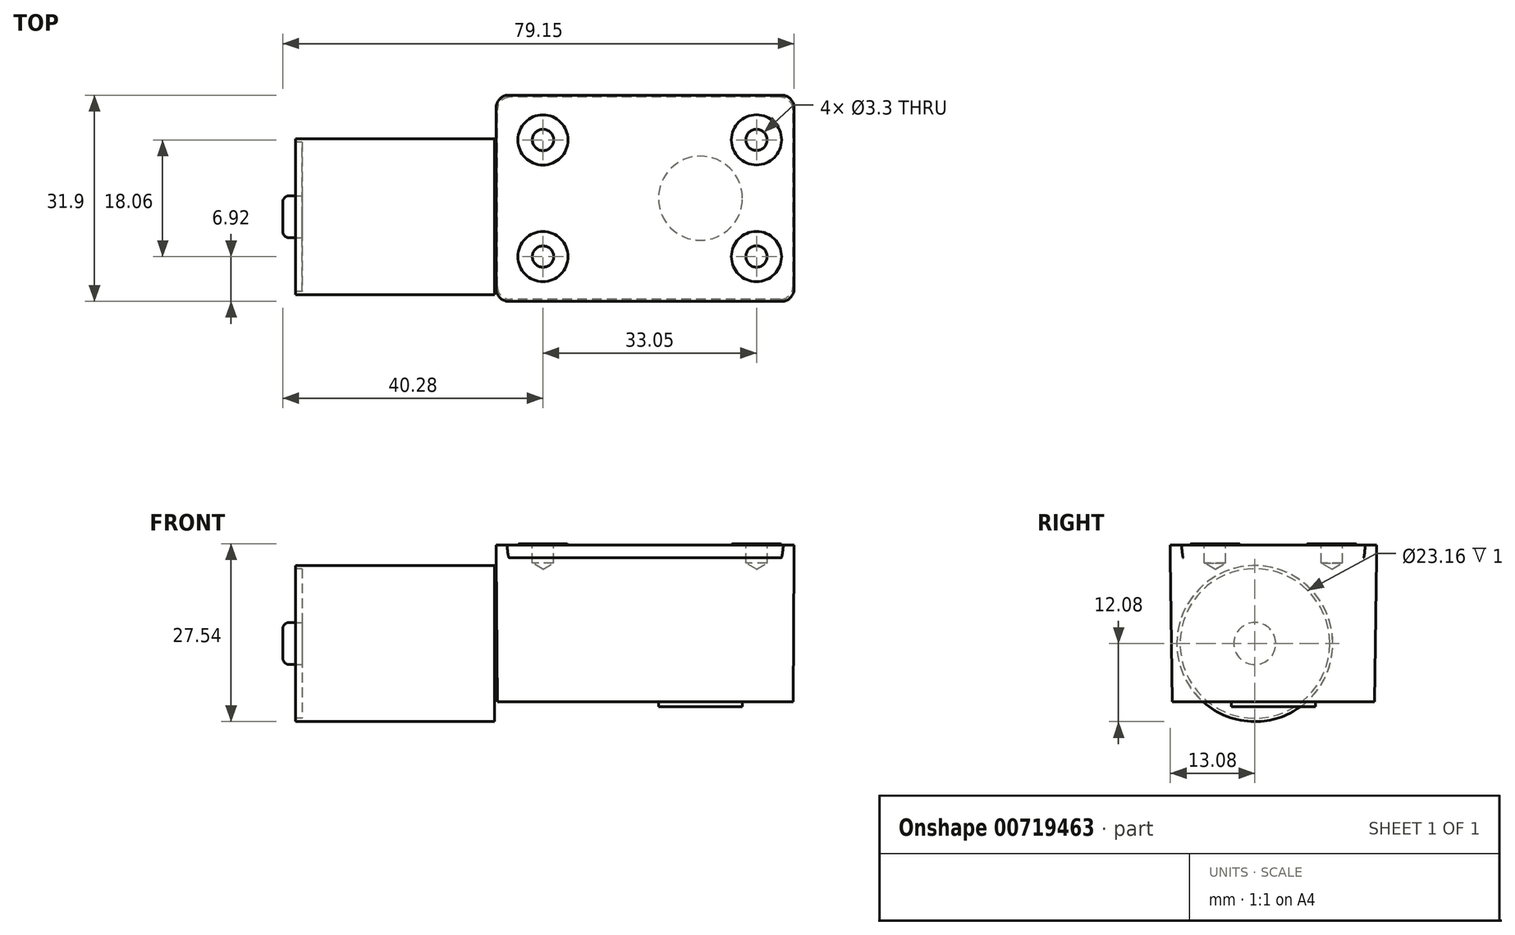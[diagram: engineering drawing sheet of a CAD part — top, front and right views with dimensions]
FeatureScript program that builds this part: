
annotation { "Feature Type Name" : "Feature", "Feature Type Description" : "" }
export const myFeature = defineFeature(function(context is Context, id is Id, definition is map)
    precondition{}
    {
        {
            var Q0;
            Q0=qCreatedBy(makeId("Top.planeOp"),FACE);
            var sketch = newSketch(context, id + "F0", { "sketchPlane" : qUnion([Q0])});
            skPoint(sketch, "E0.middle", {"position": v(0, 0) * mm});
            skPoint(sketch, "E1.middle", {"position": v(1.24, 0) * mm});
            skLineSegment(sketch, "E2.bottom", {"start": v(22.88, -15.65) * mm, "end": v(-22.88, -15.65) * mm});
            skLineSegment(sketch, "E2.top", {"start": v(22.88, 15.65) * mm, "end": v(-22.88, 15.65) * mm});
            skLineSegment(sketch, "E2.left", {"start": v(22.88, -15.65) * mm, "end": v(22.88, 15.65) * mm});
            skLineSegment(sketch, "E2.right", {"start": v(-22.88, -15.65) * mm, "end": v(-22.88, 15.65) * mm});
            skSolve(sketch);
        }
        {
            var Q0;
            Q0=qCreatedBy(makeId("Top.planeOp"),FACE);
            cPlane(context, id + "F1", {"entities" : qUnion([Q0]), "cplaneType" : CPlaneType.OFFSET, "offset" : 22.3 * mm, "width" : 150 * mm, "height" : 150 * mm});
        }
        {
            var Q0;
            Q0=qCreatedBy(id+"F1.planeOp",FACE);
            var sketch = newSketch(context, id + "F2", { "sketchPlane" : qUnion([Q0])});
            skLineSegment(sketch, "E3.bottom", {"start": v(23.05, -15.95) * mm, "end": v(-23.05, -15.95) * mm});
            skLineSegment(sketch, "E3.top", {"start": v(23.05, 15.95) * mm, "end": v(-23.05, 15.95) * mm});
            skLineSegment(sketch, "E3.left", {"start": v(23.05, -15.95) * mm, "end": v(23.05, 15.95) * mm});
            skLineSegment(sketch, "E3.right", {"start": v(-23.05, -15.95) * mm, "end": v(-23.05, 15.95) * mm});
            skPoint(sketch, "E3.middle", {"position": v(0, 0) * mm});
            skLineSegment(sketch, "E4.bottom", {"start": v(-23.3, -14.95) * mm, "end": v(-54.1, -14.95) * mm});
            skLineSegment(sketch, "E4.top", {"start": v(-23.3, -2.88) * mm, "end": v(-54.1, -2.88) * mm});
            skLineSegment(sketch, "E4.left", {"start": v(-23.3, -14.95) * mm, "end": v(-23.3, -2.88) * mm});
            skLineSegment(sketch, "E4.right", {"start": v(-54.1, -14.95) * mm, "end": v(-54.1, -2.88) * mm});
            skPoint(sketch, "E4.middle", {"position": v(-38.7, -8.91) * mm});
            skSolve(sketch);
        }
        {
            var Q0;
            Q0=makeQuery(id+"F0.imprint","IMPRINT",FACE,{"disambiguationData":[TD([[makeQuery(id+"F0.imprint","IMPRINT",EDGE,{"derivedFrom":sQuery(id+"F0.wireOp",EDGE,"E2.bottom")}),-1.0]])]});
            var Q1;
            Q1=makeQuery(id+"F2.imprint","IMPRINT",FACE,{"disambiguationData":[TD([[makeQuery(id+"F2.imprint","IMPRINT",EDGE,{"derivedFrom":sQuery(id+"F2.wireOp",EDGE,"E3.bottom")}),-1.0]])]});
            loft(context, id + "F3", {"sheetProfilesArray" : [{ "sheetProfileEntities" : qUnion([Q0]) }, { "sheetProfileEntities" : qUnion([Q1]) }]});
        }
        {
            var Q0;
            Q0=makeQuery(id+"F2.imprint","IMPRINT",FACE,{"disambiguationData":[TD([[makeQuery(id+"F2.imprint","IMPRINT",EDGE,{"derivedFrom":sQuery(id+"F2.wireOp",EDGE,"E4.bottom")}),-1.0]])]});
            var Q1;
            Q1=sQuery(id+"F2.wireOp",EDGE,"E4.top");
            revolve(context, id + "F4", {"surfaceOperationType" : NewSurfaceOperationType.NEW, "entities" : qUnion([Q0]), "axis" : qUnion([Q1]), "revolveType" : RevolveType.FULL});
        }
        {
            var Q0;
            Q0=makeQuery(id+"F4.opRevolve","SWEPT_BODY",BODY,{"disambiguationData":[OSD([sQuery(id+"F2.wireOp",EDGE,"E4.bottom"),sQuery(id+"F2.wireOp",EDGE,"E4.top"),sQuery(id+"F2.wireOp",EDGE,"E4.left"),sQuery(id+"F2.wireOp",EDGE,"E4.right")])]});
            transform(context, id + "F5", {"entities" : qUnion([Q0]), "transformType" : TransformType.TRANSLATION_3D, "dx" : 0 * mm, "dy" : 0 * mm, "dz" : -13.27 * mm, "makeCopy" : false});
        }
        {
            var Q0;
            Q0=makeQuery(id+"F4.opRevolve","SWEPT_FACE",FACE,{"disambiguationData":[OSD([sQuery(id+"F2.wireOp",EDGE,"E4.right")])]});
            var sketch = newSketch(context, id + "F6", { "sketchPlane" : qUnion([Q0])});
            skCircle(sketch, "E5", {"center": v(2.87, 9.04) * mm, "radius": 3.25 * mm});
            skCircle(sketch, "E6", {"center": v(2.87, 9.04) * mm, "radius": 11.58 * mm});
            skSolve(sketch);
        }
        {
            var Q0;
            Q0=makeQuery(id+"F6.imprint","IMPRINT",FACE,{"disambiguationData":[TD([[makeQuery(id+"F6.imprint","IMPRINT",EDGE,{"derivedFrom":sQuery(id+"F6.wireOp",EDGE,"E5")}),1.0]])]});
            extrude(context, id + "F7", {"entities" : qUnion([Q0]), "operationType" : NewBodyOperationType.ADD, "depth" : 2 * mm, "offsetDistance" : 25 * mm});
        }
        {
            var Q0;
            Q0 = qSketchRegion(id + "F6", true);
            extrude(context, id + "F8", {"entities" : qUnion([Q0]), "operationType" : NewBodyOperationType.REMOVE, "oppositeDirection" : true, "depth" : 1 * mm, "offsetDistance" : 25 * mm});
        }
        {
            var Q0;
            Q0=makeQuery(id+"F2.imprint","IMPRINT",FACE,{"disambiguationData":[TD([[makeQuery(id+"F2.imprint","IMPRINT",EDGE,{"derivedFrom":sQuery(id+"F2.wireOp",EDGE,"E3.bottom")}),-1.0]])]});
            var sketch = newSketch(context, id + "F9", { "sketchPlane" : qUnion([Q0])});
            skCircle(sketch, "E7", {"center": v(17.23, 9.03) * mm, "radius": 3.88 * mm});
            skCircle(sketch, "E8", {"center": v(17.23, -9.02) * mm, "radius": 3.88 * mm});
            skCircle(sketch, "E9", {"center": v(-15.82, 9.02) * mm, "radius": 3.88 * mm});
            skCircle(sketch, "E10", {"center": v(-15.82, -9.03) * mm, "radius": 3.88 * mm});
            skCircle(sketch, "E11", {"center": v(-4.62, 5) * mm, "radius": 3 * mm});
            skCircle(sketch, "E12", {"center": v(-4.68, -5) * mm, "radius": 3 * mm});
            skLineSegment(sketch, "E13", {"start": v(-7.62, 5.11) * mm, "end": v(-7.68, -4.98) * mm});
            skLineSegment(sketch, "E14", {"start": v(-1.63, 5.2) * mm, "end": v(-1.68, -5.01) * mm});
            skSolve(sketch);
        }
        {
            var Q0;
            Q0=makeQuery(id+"F9.imprint","IMPRINT",FACE,{"disambiguationData":[TD([[makeQuery(id+"F9.imprint","IMPRINT",EDGE,{"derivedFrom":sQuery(id+"F9.wireOp",EDGE,"E9")}),1.0]])]});
            var Q1;
            Q1=makeQuery(id+"F9.imprint","IMPRINT",FACE,{"disambiguationData":[TD([[makeQuery(id+"F9.imprint","IMPRINT",EDGE,{"derivedFrom":sQuery(id+"F9.wireOp",EDGE,"E10")}),1.0]])]});
            var Q2;
            Q2=makeQuery(id+"F9.imprint","IMPRINT",FACE,{"disambiguationData":[TD([[makeQuery(id+"F9.imprint","IMPRINT",EDGE,{"derivedFrom":sQuery(id+"F9.wireOp",EDGE,"E7")}),1.0]])]});
            var Q3;
            Q3=makeQuery(id+"F9.imprint","IMPRINT",FACE,{"disambiguationData":[TD([[makeQuery(id+"F9.imprint","IMPRINT",EDGE,{"derivedFrom":sQuery(id+"F9.wireOp",EDGE,"E8")}),1.0]])]});
            extrude(context, id + "F10", {"entities" : qUnion([Q0, Q1, Q2, Q3]), "operationType" : NewBodyOperationType.ADD, "depth" : 2.2 * mm, "offsetDistance" : 25 * mm});
        }
        {
            var Q0;
            Q0=makeQuery(id+"F10.opExtrude","CAP_FACE",FACE,{"disambiguationData":[OSD([sQuery(id+"F9.wireOp",EDGE,"E9")])],"isStart":false});
            var sketch = newSketch(context, id + "F11", { "sketchPlane" : qUnion([Q0])});
            skPoint(sketch, "E15", {"position": v(-15.82, 9.02) * mm});
            skSolve(sketch);
        }
        {
            var Q0;
            Q0=makeQuery(id+"F10.opExtrude","CAP_FACE",FACE,{"disambiguationData":[OSD([sQuery(id+"F9.wireOp",EDGE,"E7")])],"isStart":false});
            var sketch = newSketch(context, id + "F12", { "sketchPlane" : qUnion([Q0])});
            skPoint(sketch, "E16", {"position": v(17.23, 9.03) * mm});
            skSolve(sketch);
        }
        {
            var Q0;
            Q0=makeQuery(id+"F10.opExtrude","CAP_FACE",FACE,{"disambiguationData":[OSD([sQuery(id+"F9.wireOp",EDGE,"E10")])],"isStart":false});
            var sketch = newSketch(context, id + "F13", { "sketchPlane" : qUnion([Q0])});
            skPoint(sketch, "E17", {"position": v(-15.82, -9.03) * mm});
            skSolve(sketch);
        }
        {
            var Q0;
            Q0=makeQuery(id+"F10.opExtrude","CAP_FACE",FACE,{"disambiguationData":[OSD([sQuery(id+"F9.wireOp",EDGE,"E8")])],"isStart":false});
            var sketch = newSketch(context, id + "F14", { "sketchPlane" : qUnion([Q0])});
            skPoint(sketch, "E18", {"position": v(17.23, -9.02) * mm});
            skSolve(sketch);
        }
        {
            var Q0;
            Q0=sQuery(id+"F11.wireOp",VERTEX,"E15");
            var Q1;
            Q1=sQuery(id+"F13.wireOp",VERTEX,"E17");
            var Q2;
            Q2=sQuery(id+"F12.wireOp",VERTEX,"E16");
            var Q3;
            Q3=sQuery(id+"F14.wireOp",VERTEX,"E18");
            var Q4;
            Q4=makeQuery(id+"F3.opLoft","SWEPT_BODY",BODY,{"disambiguationData":[OSD([makeQuery(id+"F0.imprint","IMPRINT",FACE,{"disambiguationData":[TD([[makeQuery(id+"F0.imprint","IMPRINT",EDGE,{"derivedFrom":sQuery(id+"F0.wireOp",EDGE,"E2.bottom")}),-1.0]])]}),makeQuery(id+"F2.imprint","IMPRINT",FACE,{"disambiguationData":[TD([[makeQuery(id+"F2.imprint","IMPRINT",EDGE,{"derivedFrom":sQuery(id+"F2.wireOp",EDGE,"E3.bottom")}),-1.0]])]})])]});
            hole(context, id + "F15", {"style" : HoleStyle.SIMPLE, "endStyle" : HoleEndStyle.BLIND, "standardTappedOrClearance" : lookupTablePath({ "standard" : "ISO", "fit" : "Normal", "size" : "M3", "type" : "Clearance" }), "standardBlindInLast" : lookupTablePath({ "fit" : "Standard", "standard" : "ISO", "size" : "M3", "type" : "Clearance" }), "holeDiameter" : 3.3 * mm, "majorDiameter" : 5 * mm, "holeDepth" : 3 * mm, "isTappedThrough" : true, "tappedDepth" : 12 * mm, "tapClearance" : 3, "locations" : qUnion([Q0, Q1, Q2, Q3]), "scope" : qUnion([Q4])});
        }
        {
            var Q0;
            Q0=makeQuery(id+"F2.imprint","IMPRINT",FACE,{"disambiguationData":[TD([[makeQuery(id+"F2.imprint","IMPRINT",EDGE,{"derivedFrom":sQuery(id+"F2.wireOp",EDGE,"E3.bottom")}),-1.0]])]});
            var sketch = newSketch(context, id + "F16", { "sketchPlane" : qUnion([Q0])});
            skCircle(sketch, "E19", {"center": v(8.55, 0) * mm, "radius": 6.67 * mm});
            skCircle(sketch, "E20", {"center": v(8.55, 0) * mm, "radius": 3 * mm});
            skSolve(sketch);
        }
        {
            var Q0;
            Q0=makeQuery(id+"F16.imprint","IMPRINT",FACE,{"disambiguationData":[TD([[makeQuery(id+"F16.imprint","IMPRINT",EDGE,{"derivedFrom":sQuery(id+"F16.wireOp",EDGE,"E19")}),1.0]])]});
            extrude(context, id + "F17", {"entities" : qUnion([Q0]), "operationType" : NewBodyOperationType.ADD, "depth" : 2 * mm, "offsetDistance" : 25 * mm});
        }
        {
            var Q0;
            {var subQ0=sQuery(id+"F9.wireOp",EDGE,"E13");var subQ1=sQuery(id+"F9.wireOp",EDGE,"E11");var subQ2=makeQuery(id+"F9.imprint","INTERSECT",VERTEX,{"disambiguationData":[OD(0.0)],"derivedFrom":[subQ1,subQ0]});Q0=makeQuery(id+"F9.imprint","IMPRINT",FACE,{"disambiguationData":[TD([[makeQuery(id+"F9.imprint","IMPRINT",EDGE,{"disambiguationData":[TD([[subQ2,1.0]])],"derivedFrom":subQ1}),1.0]])]});}
            var Q1;
            {var subQ0=sQuery(id+"F9.wireOp",EDGE,"E13");var subQ1=sQuery(id+"F9.wireOp",EDGE,"E11");var subQ2=makeQuery(id+"F9.imprint","INTERSECT",VERTEX,{"disambiguationData":[OD(1.0)],"derivedFrom":[subQ1,subQ0]});Q1=makeQuery(id+"F9.imprint","IMPRINT",FACE,{"disambiguationData":[TD([[makeQuery(id+"F9.imprint","IMPRINT",EDGE,{"disambiguationData":[TD([[subQ2,-1.0]])],"derivedFrom":subQ1}),-1.0]])]});}
            var Q2;
            {var subQ0=sQuery(id+"F9.wireOp",EDGE,"E12");var subQ3=makeQuery(id+"F9.imprint","IMPRINT",VERTEX,{"derivedFrom":subQ0});Q2=makeQuery(id+"F9.imprint","IMPRINT",FACE,{"disambiguationData":[TD([[makeQuery(id+"F9.imprint","IMPRINT",EDGE,{"disambiguationData":[TD([[subQ3,1.0]])],"derivedFrom":subQ0}),1.0]])]});}
            extrude(context, id + "F18", {"entities" : qUnion([Q0, Q1, Q2]), "operationType" : NewBodyOperationType.ADD, "depth" : 2 * mm, "offsetDistance" : 25 * mm});
        }
        {
            var Q0;
            Q0=makeQuery(id+"F3.opLoft","CAP_FACE",FACE,{"disambiguationData":[OSD([makeQuery(id+"F0.imprint","IMPRINT",FACE,{"disambiguationData":[TD([[makeQuery(id+"F0.imprint","IMPRINT",EDGE,{"derivedFrom":sQuery(id+"F0.wireOp",EDGE,"E2.bottom")}),-1.0]])]})])],"isStart":true});
            var sketch = newSketch(context, id + "F19", { "sketchPlane" : qUnion([Q0])});
            skCircle(sketch, "E21", {"center": v(8.55, 0) * mm, "radius": 6.5 * mm});
            skPoint(sketch, "E21.centerSnap0", {"position": v(22.88, 0) * mm});
            skSolve(sketch);
        }
        {
            var Q0;
            Q0=makeQuery(id+"F19.imprint","IMPRINT",FACE,{"disambiguationData":[TD([[makeQuery(id+"F19.imprint","IMPRINT",EDGE,{"derivedFrom":sQuery(id+"F19.wireOp",EDGE,"E21")}),1.0]])]});
            extrude(context, id + "F20", {"entities" : qUnion([Q0]), "operationType" : NewBodyOperationType.ADD, "depth" : 0.75 * mm, "offsetDistance" : 25 * mm});
        }
        {
            var Q0;
            Q0=makeQuery(id+"F3.opLoft","SWEPT_EDGE",EDGE,{"disambiguationData":[OSD([sQuery(id+"F0.wireOp",EDGE,"E2.bottom"),sQuery(id+"F0.wireOp",EDGE,"E2.right"),sQuery(id+"F2.wireOp",EDGE,"E3.bottom"),sQuery(id+"F2.wireOp",EDGE,"E3.right")])]});
            var Q1;
            Q1=makeQuery(id+"F3.opLoft","SWEPT_EDGE",EDGE,{"disambiguationData":[OSD([sQuery(id+"F0.wireOp",EDGE,"E2.top"),sQuery(id+"F0.wireOp",EDGE,"E2.right"),sQuery(id+"F2.wireOp",EDGE,"E3.top"),sQuery(id+"F2.wireOp",EDGE,"E3.right")])]});
            var Q2;
            Q2=makeQuery(id+"F3.opLoft","SWEPT_EDGE",EDGE,{"disambiguationData":[OSD([sQuery(id+"F0.wireOp",EDGE,"E2.top"),sQuery(id+"F0.wireOp",EDGE,"E2.left"),sQuery(id+"F2.wireOp",EDGE,"E3.top"),sQuery(id+"F2.wireOp",EDGE,"E3.left")])]});
            var Q3;
            Q3=makeQuery(id+"F3.opLoft","SWEPT_EDGE",EDGE,{"disambiguationData":[OSD([sQuery(id+"F0.wireOp",EDGE,"E2.bottom"),sQuery(id+"F0.wireOp",EDGE,"E2.left"),sQuery(id+"F2.wireOp",EDGE,"E3.bottom"),sQuery(id+"F2.wireOp",EDGE,"E3.left")])]});
            fillet(context, id + "F21", {"entities" : qUnion([Q0, Q1, Q2, Q3]), "radius" : 2 * mm, "tangentPropagation" : true, "allowEdgeOverflow" : false});
        }
        {
            var Q0;
            Q0=makeQuery(id+"F10.opExtrude","CAP_EDGE",EDGE,{"disambiguationData":[OSD([sQuery(id+"F9.wireOp",EDGE,"E9")])],"isStart":false});
            var Q1;
            Q1=makeQuery(id+"F10.opExtrude","CAP_EDGE",EDGE,{"disambiguationData":[OSD([sQuery(id+"F9.wireOp",EDGE,"E10")])],"isStart":false});
            var Q2;
            Q2=makeQuery(id+"F10.opExtrude","CAP_EDGE",EDGE,{"disambiguationData":[OSD([sQuery(id+"F9.wireOp",EDGE,"E7")])],"isStart":false});
            var Q3;
            Q3=makeQuery(id+"F10.opExtrude","CAP_EDGE",EDGE,{"disambiguationData":[OSD([sQuery(id+"F9.wireOp",EDGE,"E8")])],"isStart":false});
            var Q4;
            Q4=makeQuery(id+"F18.opExtrude","CAP_EDGE",EDGE,{"disambiguationData":[OSD([sQuery(id+"F9.wireOp",EDGE,"E14")])],"isStart":false});
            var Q5;
            Q5=makeQuery(id+"F18.opExtrude","CAP_EDGE",EDGE,{"disambiguationData":[OSD([sQuery(id+"F9.wireOp",EDGE,"E11")])],"isStart":false});
            var Q6;
            Q6=makeQuery(id+"F18.opExtrude","CAP_EDGE",EDGE,{"disambiguationData":[OSD([sQuery(id+"F9.wireOp",EDGE,"E13")])],"isStart":false});
            var Q7;
            Q7=makeQuery(id+"F18.opExtrude","CAP_FACE",FACE,{"disambiguationData":[OSD([sQuery(id+"F9.wireOp",EDGE,"E11"),sQuery(id+"F9.wireOp",EDGE,"E12"),sQuery(id+"F9.wireOp",EDGE,"E13"),sQuery(id+"F9.wireOp",EDGE,"E14")])],"isStart":false});
            var Q8;
            Q8=makeQuery(id+"F17.opExtrude","CAP_EDGE",EDGE,{"disambiguationData":[OSD([sQuery(id+"F16.wireOp",EDGE,"E19")])],"isStart":false});
            fillet(context, id + "F22", {"entities" : qUnion([Q0, Q1, Q2, Q3, Q4, Q5, Q6, Q7, Q8]), "radius" : .33 * mm, "tangentPropagation" : true, "allowEdgeOverflow" : false});
        }
        {
            var Q0;
            Q0=makeQuery(id+"F7.opExtrude","CAP_EDGE",EDGE,{"disambiguationData":[OSD([sQuery(id+"F6.wireOp",EDGE,"E5")])],"isStart":false});
            fillet(context, id + "F23", {"entities" : qUnion([Q0]), "radius" : 1 * mm, "tangentPropagation" : true, "allowEdgeOverflow" : false});
        }
    });
